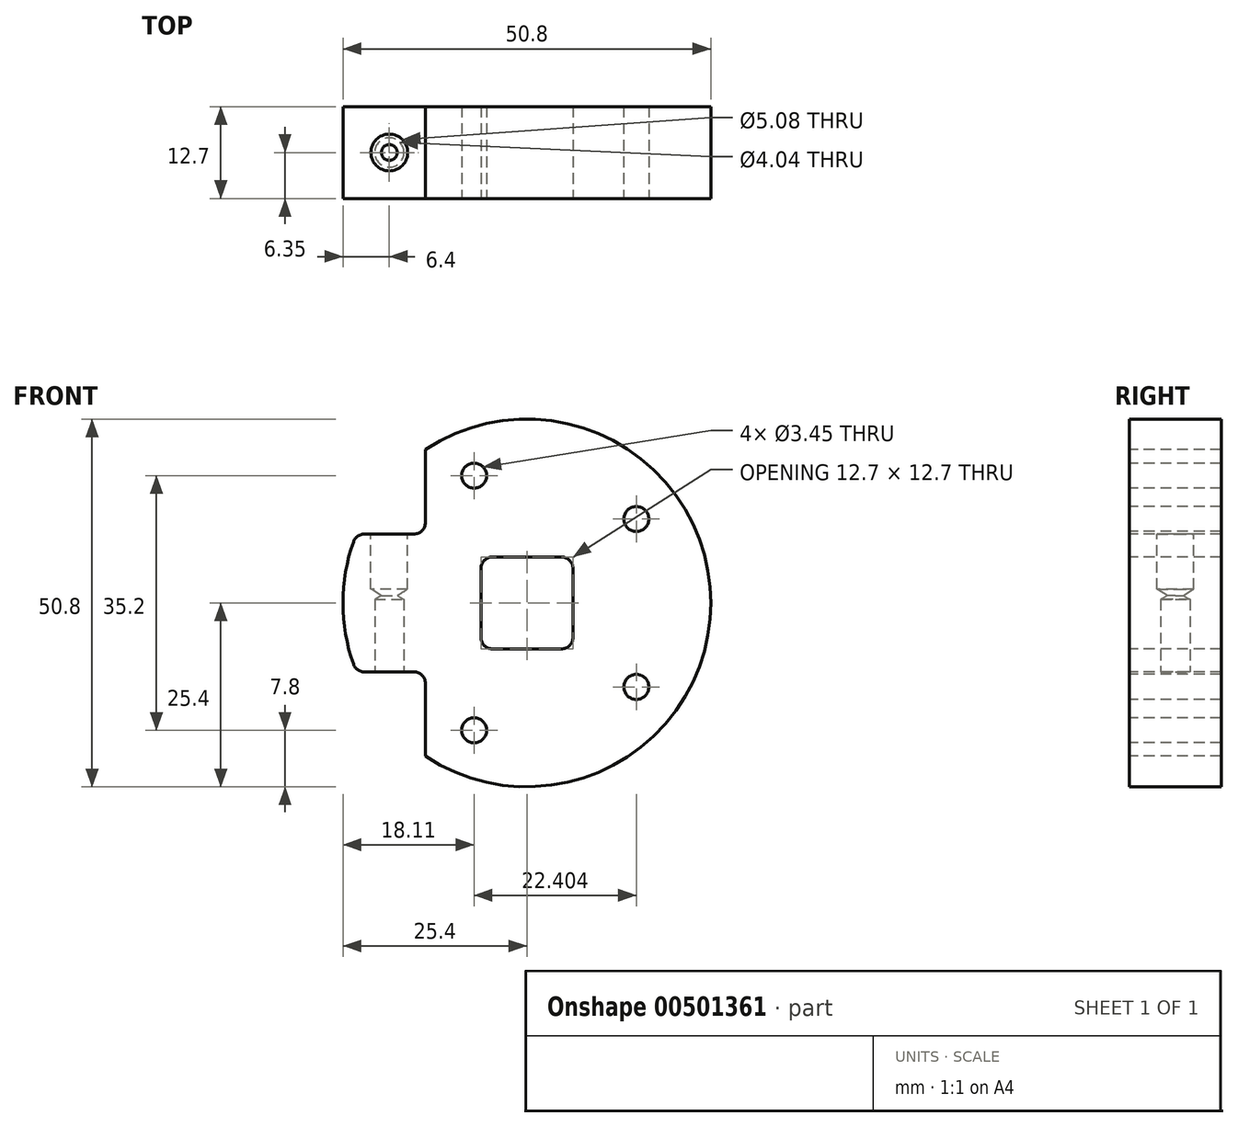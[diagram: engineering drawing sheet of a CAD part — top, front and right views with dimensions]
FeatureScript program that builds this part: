
annotation { "Feature Type Name" : "Feature", "Feature Type Description" : "" }
export const myFeature = defineFeature(function(context is Context, id is Id, definition is map)
    precondition{}
    {
        {
            var Q0;
            Q0=qCreatedBy(makeId("Front.planeOp"),FACE);
            var sketch = newSketch(context, id + "F0", { "sketchPlane" : qUnion([Q0])});
            skCircle(sketch, "E0", {"center": v(0, 0) * mm, "radius": 25.4 * mm});
            skSolve(sketch);
        }
        {
            var Q0;
            Q0=makeQuery(id+"F0.imprint","IMPRINT",FACE,{"disambiguationData":[TD([[makeQuery(id+"F0.imprint","IMPRINT",EDGE,{"derivedFrom":sQuery(id+"F0.wireOp",EDGE,"E0")}),1.0]])]});
            extrude(context, id + "F1", {"entities" : qUnion([Q0]), "endBound" : BoundingType.SYMMETRIC, "depth" : 12.7 * mm});
        }
        {
            var Q0;
            Q0=makeQuery(id+"F1.opExtrude","CAP_FACE",FACE,{"disambiguationData":[OSD([sQuery(id+"F0.wireOp",EDGE,"E0")])],"isStart":false});
            var sketch = newSketch(context, id + "F2", { "sketchPlane" : qUnion([Q0])});
            skLineSegment(sketch, "E1.bottom", {"start": v(-6.35, 6.35) * mm, "end": v(6.35, 6.35) * mm});
            skLineSegment(sketch, "E1.top", {"start": v(-6.35, -6.35) * mm, "end": v(6.35, -6.35) * mm});
            skLineSegment(sketch, "E1.left", {"start": v(-6.35, 6.35) * mm, "end": v(-6.35, -6.35) * mm});
            skLineSegment(sketch, "E1.right", {"start": v(6.35, 6.35) * mm, "end": v(6.35, -6.35) * mm});
            skLineSegment(sketch, "E2.bottom", {"start": v(-6.35, -1.59) * mm, "end": v(-25.4, -1.59) * mm});
            skLineSegment(sketch, "E2.top", {"start": v(-6.35, 1.59) * mm, "end": v(-25.4, 1.59) * mm});
            skLineSegment(sketch, "E2.left", {"start": v(-6.35, -1.59) * mm, "end": v(-6.35, 1.59) * mm});
            skLineSegment(sketch, "E2.right", {"start": v(-25.4, -1.59) * mm, "end": v(-25.4, 1.59) * mm});
            skSolve(sketch);
        }
        {
            var Q0;
            {var subQ4=sQuery(id+"F2.wireOp",EDGE,"E2.left");Q0=makeQuery(id+"F2.imprint","IMPRINT",FACE,{"disambiguationData":[TD([[makeQuery(id+"F2.imprint","IMPRINT",EDGE,{"derivedFrom":subQ4}),1.0]])]});}
            var Q1;
            {var subQ3=sQuery(id+"F2.wireOp",EDGE,"E1.bottom");Q1=makeQuery(id+"F2.imprint","IMPRINT",FACE,{"disambiguationData":[TD([[makeQuery(id+"F2.imprint","IMPRINT",EDGE,{"derivedFrom":subQ3}),-1.0]])]});}
            extrude(context, id + "F3", {"entities" : qUnion([Q0, Q1]), "operationType" : NewBodyOperationType.REMOVE, "oppositeDirection" : true, "depth" : 25.4 * mm});
        }
        {
            var Q0;
            Q0=makeQuery(id+"F1.opExtrude","CAP_FACE",FACE,{"disambiguationData":[OSD([sQuery(id+"F0.wireOp",EDGE,"E0")])],"isStart":false});
            var sketch = newSketch(context, id + "F4", { "sketchPlane" : qUnion([Q0])});
            skLineSegment(sketch, "E3.bottom", {"start": v(-14.02, 9.53) * mm, "end": v(-23.55, 9.53) * mm});
            skLineSegment(sketch, "E3.top", {"start": v(-14.02, 21.18) * mm, "end": v(-23.55, 21.18) * mm});
            skLineSegment(sketch, "E3.left", {"start": v(-14.02, 9.53) * mm, "end": v(-14.02, 21.18) * mm});
            skLineSegment(sketch, "E3.right", {"start": v(-23.55, 9.53) * mm, "end": v(-23.55, 21.18) * mm});
            skLineSegment(sketch, "E4.bottom", {"start": v(-14.02, -9.53) * mm, "end": v(-23.55, -9.53) * mm});
            skLineSegment(sketch, "E4.top", {"start": v(-14.02, -21.18) * mm, "end": v(-23.55, -21.18) * mm});
            skLineSegment(sketch, "E4.left", {"start": v(-14.02, -9.53) * mm, "end": v(-14.02, -21.18) * mm});
            skLineSegment(sketch, "E4.right", {"start": v(-23.55, -9.53) * mm, "end": v(-23.55, -21.18) * mm});
            skSolve(sketch);
        }
        {
            var Q0;
            {var subQ0=sQuery(id+"F4.wireOp",EDGE,"E3.bottom");Q0=makeQuery(id+"F4.imprint","IMPRINT",FACE,{"disambiguationData":[TD([[makeQuery(id+"F4.imprint","IMPRINT",EDGE,{"derivedFrom":subQ0}),-1.0]])]});}
            var Q1;
            {var subQ0=sQuery(id+"F4.wireOp",EDGE,"E4.bottom");Q1=makeQuery(id+"F4.imprint","IMPRINT",FACE,{"disambiguationData":[TD([[makeQuery(id+"F4.imprint","IMPRINT",EDGE,{"derivedFrom":subQ0}),1.0]])]});}
            extrude(context, id + "F5", {"entities" : qUnion([Q0, Q1]), "operationType" : NewBodyOperationType.REMOVE, "oppositeDirection" : true, "depth" : 25.4 * mm});
        }
        {
            var Q0;
            Q0=makeQuery(id+"F5.boolean.opBoolean","COPY",EDGE,{"derivedFrom":makeQuery(id+"F5.opExtrude","SWEPT_EDGE",EDGE,{"disambiguationData":[OSD([sQuery(id+"F0.wireOp",EDGE,"E0"),sQuery(id+"F4.wireOp",EDGE,"E3.bottom"),sQuery(id+"F4.wireOp",EDGE,"E3.right")])]})});
            var Q1;
            Q1=makeQuery(id+"F5.boolean.opBoolean","COPY",EDGE,{"derivedFrom":makeQuery(id+"F5.opExtrude","SWEPT_EDGE",EDGE,{"disambiguationData":[OSD([sQuery(id+"F0.wireOp",EDGE,"E0"),sQuery(id+"F4.wireOp",EDGE,"E3.top"),sQuery(id+"F4.wireOp",EDGE,"E3.left")])]})});
            var Q2;
            Q2=makeQuery(id+"F5.boolean.opBoolean","COPY",EDGE,{"derivedFrom":makeQuery(id+"F5.opExtrude","SWEPT_EDGE",EDGE,{"disambiguationData":[OSD([sQuery(id+"F4.wireOp",EDGE,"E3.bottom"),sQuery(id+"F4.wireOp",EDGE,"E3.left")])]})});
            var Q3;
            Q3=makeQuery(id+"F3.boolean.opBoolean","COPY",EDGE,{"derivedFrom":makeQuery(id+"F3.opExtrude","SWEPT_EDGE",EDGE,{"disambiguationData":[OSD([sQuery(id+"F2.wireOp",EDGE,"E1.bottom"),sQuery(id+"F2.wireOp",EDGE,"E1.left")])]})});
            var Q4;
            Q4=makeQuery(id+"F3.boolean.opBoolean","COPY",EDGE,{"derivedFrom":makeQuery(id+"F3.opExtrude","SWEPT_EDGE",EDGE,{"disambiguationData":[OSD([sQuery(id+"F2.wireOp",EDGE,"E1.left"),sQuery(id+"F2.wireOp",EDGE,"E2.top"),sQuery(id+"F2.wireOp",EDGE,"E2.left")])]})});
            var Q5;
            Q5=makeQuery(id+"F3.boolean.opBoolean","COPY",EDGE,{"derivedFrom":makeQuery(id+"F3.opExtrude","SWEPT_EDGE",EDGE,{"disambiguationData":[OSD([sQuery(id+"F2.wireOp",EDGE,"E1.left"),sQuery(id+"F2.wireOp",EDGE,"E2.bottom"),sQuery(id+"F2.wireOp",EDGE,"E2.left")])]})});
            var Q6;
            Q6=makeQuery(id+"F3.boolean.opBoolean","COPY",EDGE,{"derivedFrom":makeQuery(id+"F3.opExtrude","SWEPT_EDGE",EDGE,{"disambiguationData":[OSD([sQuery(id+"F2.wireOp",EDGE,"E1.top"),sQuery(id+"F2.wireOp",EDGE,"E1.left")])]})});
            var Q7;
            Q7=makeQuery(id+"F3.boolean.opBoolean","COPY",EDGE,{"derivedFrom":makeQuery(id+"F3.opExtrude","SWEPT_EDGE",EDGE,{"disambiguationData":[OSD([sQuery(id+"F2.wireOp",EDGE,"E1.bottom"),sQuery(id+"F2.wireOp",EDGE,"E1.right")])]})});
            var Q8;
            Q8=makeQuery(id+"F3.boolean.opBoolean","COPY",EDGE,{"derivedFrom":makeQuery(id+"F3.opExtrude","SWEPT_EDGE",EDGE,{"disambiguationData":[OSD([sQuery(id+"F2.wireOp",EDGE,"E1.top"),sQuery(id+"F2.wireOp",EDGE,"E1.right")])]})});
            var Q9;
            Q9=makeQuery(id+"F5.boolean.opBoolean","COPY",EDGE,{"derivedFrom":makeQuery(id+"F5.opExtrude","SWEPT_EDGE",EDGE,{"disambiguationData":[OSD([sQuery(id+"F0.wireOp",EDGE,"E0"),sQuery(id+"F4.wireOp",EDGE,"E4.bottom"),sQuery(id+"F4.wireOp",EDGE,"E4.right")])]})});
            var Q10;
            Q10=makeQuery(id+"F5.boolean.opBoolean","COPY",EDGE,{"derivedFrom":makeQuery(id+"F5.opExtrude","SWEPT_EDGE",EDGE,{"disambiguationData":[OSD([sQuery(id+"F4.wireOp",EDGE,"E4.bottom"),sQuery(id+"F4.wireOp",EDGE,"E4.left")])]})});
            var Q11;
            Q11=makeQuery(id+"F5.boolean.opBoolean","COPY",EDGE,{"derivedFrom":makeQuery(id+"F5.opExtrude","SWEPT_EDGE",EDGE,{"disambiguationData":[OSD([sQuery(id+"F0.wireOp",EDGE,"E0"),sQuery(id+"F4.wireOp",EDGE,"E4.top"),sQuery(id+"F4.wireOp",EDGE,"E4.left")])]})});
            fillet(context, id + "F6", {"entities" : qUnion([Q0, Q1, Q2, Q3, Q4, Q5, Q6, Q7, Q8, Q9, Q10, Q11]), "radius" : 1.59 * mm, "tangentPropagation" : true, "allowEdgeOverflow" : false});
        }
        {
            var Q0;
            Q0=makeQuery(id+"F1.opExtrude","CAP_FACE",FACE,{"disambiguationData":[OSD([sQuery(id+"F0.wireOp",EDGE,"E0")])],"isStart":false});
            var sketch = newSketch(context, id + "F7", { "sketchPlane" : qUnion([Q0])});
            skPoint(sketch, "E5", {"position": v(-7.3, 17.6) * mm});
            skLineSegment(sketch, "E6", {"start": v(-7.3, 17.6) * mm, "end": v(0, 0) * mm, "construction": true});
            skPoint(sketch, "E7", {"position": v(15.11, 11.6) * mm});
            skPoint(sketch, "E8", {"position": v(15.11, -11.6) * mm});
            skPoint(sketch, "E9", {"position": v(-7.3, -17.6) * mm});
            skLineSegment(sketch, "E10", {"start": v(0, 0) * mm, "end": v(15.11, 11.6) * mm, "construction": true});
            skLineSegment(sketch, "E11", {"start": v(0, 0) * mm, "end": v(15.11, -11.6) * mm, "construction": true});
            skLineSegment(sketch, "E12", {"start": v(0, 0) * mm, "end": v(-7.3, -17.6) * mm, "construction": true});
            skSolve(sketch);
        }
        {
            var Q0;
            Q0=sQuery(id+"F7.wireOp",VERTEX,"E5");
            var Q1;
            Q1=sQuery(id+"F7.wireOp",VERTEX,"E7");
            var Q2;
            Q2=sQuery(id+"F7.wireOp",VERTEX,"E8");
            var Q3;
            Q3=sQuery(id+"F7.wireOp",VERTEX,"E9");
            var Q4;
            Q4=makeQuery(id+"F1.opExtrude","SWEPT_BODY",BODY,{"disambiguationData":[OSD([sQuery(id+"F0.wireOp",EDGE,"E0")])]});
            hole(context, id + "F8", {"style" : HoleStyle.SIMPLE, "endStyle" : HoleEndStyle.THROUGH, "standardTappedOrClearance" : lookupTablePath({ "standard" : "ANSI", "engagement" : "75%", "pitch" : "32 tpi", "size" : "#8", "type" : "Tapped" }), "standardBlindInLast" : lookupTablePath({ "standard" : "ANSI", "engagement" : "75%", "pitch" : "32 tpi", "size" : "#8", "type" : "Tapped" }), "holeDiameter" : 3.45 * mm, "showTappedDepth" : true, "isTappedThrough" : true, "tappedDepth" : 12.7 * mm, "tapClearance" : 3, "locations" : qUnion([Q0, Q1, Q2, Q3]), "scope" : qUnion([Q4]), "majorDiameter" : 4.17 * mm});
        }
        {
            var Q0;
            Q0=makeQuery(id+"F5.boolean.opBoolean","COPY",FACE,{"derivedFrom":makeQuery(id+"F5.opExtrude","SWEPT_FACE",FACE,{"disambiguationData":[OSD([sQuery(id+"F4.wireOp",EDGE,"E3.bottom")])]})});
            var sketch = newSketch(context, id + "F9", { "sketchPlane" : qUnion([Q0])});
            skPoint(sketch, "E13", {"position": v(-19, 0) * mm});
            skSolve(sketch);
        }
        {
            var Q0;
            Q0=sQuery(id+"F9.wireOp",VERTEX,"E13");
            var Q1;
            Q1=makeQuery(id+"F1.opExtrude","SWEPT_BODY",BODY,{"disambiguationData":[OSD([sQuery(id+"F0.wireOp",EDGE,"E0")])]});
            hole(context, id + "F10", {"style" : HoleStyle.SIMPLE, "endStyle" : HoleEndStyle.BLIND, "holeDiameter" : 5.08 * mm, "holeDepth" : 7.62 * mm, "isTappedThrough" : true, "tappedDepth" : 12.7 * mm, "tapClearance" : 3, "locations" : qUnion([Q0]), "scope" : qUnion([Q1])});
        }
        {
            var Q0;
            Q0=makeQuery(id+"F5.boolean.opBoolean","COPY",FACE,{"derivedFrom":makeQuery(id+"F5.opExtrude","SWEPT_FACE",FACE,{"disambiguationData":[OSD([sQuery(id+"F4.wireOp",EDGE,"E4.bottom")])]})});
            var sketch = newSketch(context, id + "F11", { "sketchPlane" : qUnion([Q0])});
            skPoint(sketch, "E14", {"position": v(-19, 0) * mm});
            skSolve(sketch);
        }
        {
            var Q0;
            Q0=sQuery(id+"F11.wireOp",VERTEX,"E14");
            var Q1;
            Q1=makeQuery(id+"F1.opExtrude","SWEPT_BODY",BODY,{"disambiguationData":[OSD([sQuery(id+"F0.wireOp",EDGE,"E0")])]});
            hole(context, id + "F12", {"style" : HoleStyle.SIMPLE, "endStyle" : HoleEndStyle.BLIND, "standardTappedOrClearance" : lookupTablePath({ "fit" : "Normal (ASME)", "standard" : "ANSI", "engagement" : "75%", "pitch" : "32 tpi", "size" : "#10", "type" : "Tapped" }), "standardBlindInLast" : lookupTablePath({ "fit" : "Free", "standard" : "ANSI", "engagement" : "75%", "pitch" : "32 tpi", "size" : "#10", "type" : "Tapped" }), "holeDiameter" : 4.04 * mm, "showTappedDepth" : true, "holeDepth" : 10 * mm, "isTappedThrough" : true, "tappedDepth" : 7.62 * mm, "tapClearance" : 3, "locations" : qUnion([Q0]), "scope" : qUnion([Q1]), "majorDiameter" : 4.83 * mm});
        }
    });
